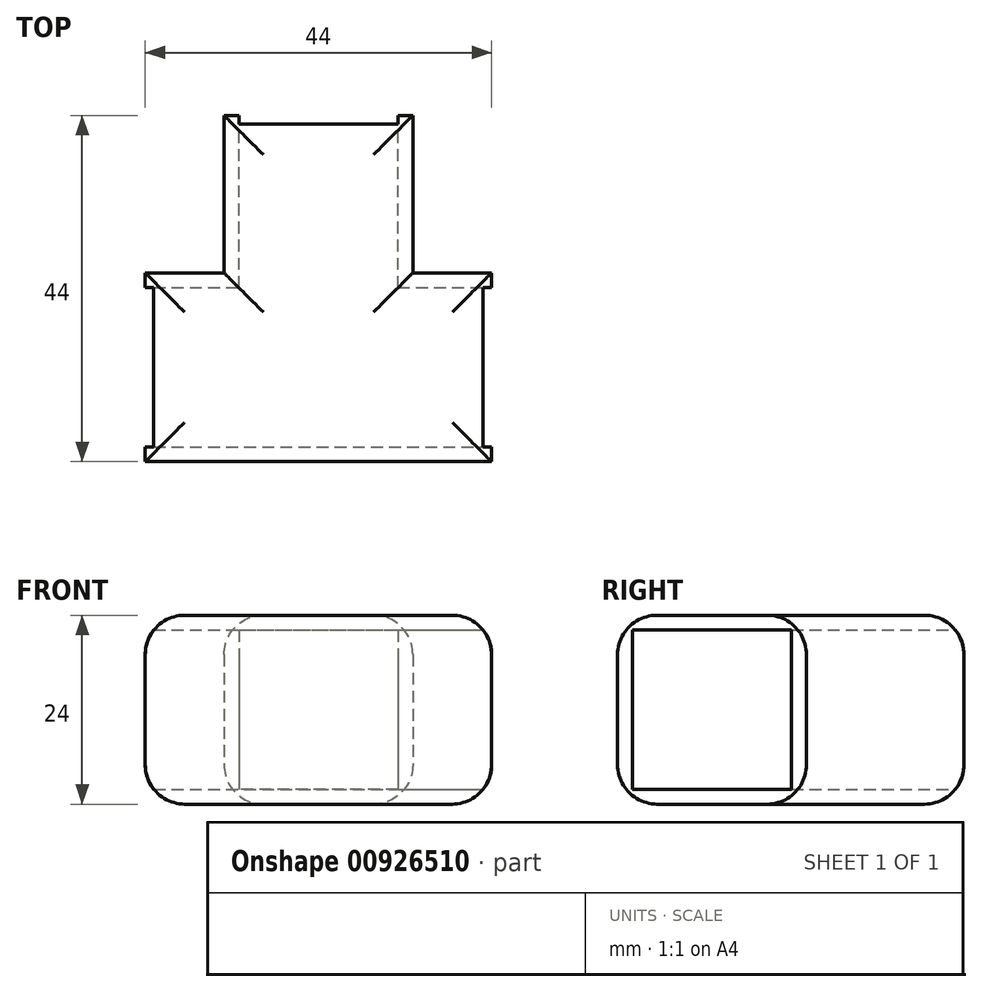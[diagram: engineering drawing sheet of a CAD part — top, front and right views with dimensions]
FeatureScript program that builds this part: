
annotation { "Feature Type Name" : "Feature", "Feature Type Description" : "" }
export const myFeature = defineFeature(function(context is Context, id is Id, definition is map)
    precondition{}
    {
        {
            var Q0;
            Q0=qCreatedBy(makeId("Top.planeOp"),FACE);
            var sketch = newSketch(context, id + "F0", { "sketchPlane" : qUnion([Q0])});
            skLineSegment(sketch, "E0.bottom", {"start": v(12.88, 0) * mm, "end": v(-11.12, 0) * mm});
            skLineSegment(sketch, "E0.top", {"start": v(12.88, 44) * mm, "end": v(-11.12, 44) * mm});
            skLineSegment(sketch, "E0.left", {"start": v(12.88, 0) * mm, "end": v(12.88, 44) * mm});
            skLineSegment(sketch, "E0.right", {"start": v(-11.12, 0) * mm, "end": v(-11.12, 44) * mm});
            skLineSegment(sketch, "E1.bottom", {"start": v(-21.12, 24) * mm, "end": v(22.88, 24) * mm});
            skLineSegment(sketch, "E1.top", {"start": v(-21.12, 0) * mm, "end": v(22.88, 0) * mm});
            skLineSegment(sketch, "E1.left", {"start": v(-21.12, 24) * mm, "end": v(-21.12, 0) * mm});
            skLineSegment(sketch, "E1.right", {"start": v(22.88, 24) * mm, "end": v(22.88, 0) * mm});
            skSolve(sketch);
        }
        {
            var Q0;
            {var subQ5=sQuery(id+"F0.wireOp",EDGE,"E1.left");Q0=makeQuery(id+"F0.imprint","IMPRINT",FACE,{"disambiguationData":[TD([[makeQuery(id+"F0.imprint","IMPRINT",EDGE,{"derivedFrom":subQ5}),1.0]])]});}
            var Q1;
            {var subQ0=sQuery(id+"F0.wireOp",EDGE,"E0.bottom");Q1=makeQuery(id+"F0.imprint","IMPRINT",FACE,{"disambiguationData":[TD([[makeQuery(id+"F0.imprint","IMPRINT",EDGE,{"derivedFrom":subQ0}),-1.0]])]});}
            var Q2;
            {var subQ5=sQuery(id+"F0.wireOp",EDGE,"E1.right");Q2=makeQuery(id+"F0.imprint","IMPRINT",FACE,{"disambiguationData":[TD([[makeQuery(id+"F0.imprint","IMPRINT",EDGE,{"derivedFrom":subQ5}),-1.0]])]});}
            var Q3;
            {var subQ0=sQuery(id+"F0.wireOp",EDGE,"E0.top");Q3=makeQuery(id+"F0.imprint","IMPRINT",FACE,{"disambiguationData":[TD([[makeQuery(id+"F0.imprint","IMPRINT",EDGE,{"derivedFrom":subQ0}),1.0]])]});}
            extrude(context, id + "F1", {"entities" : qUnion([Q0, Q1, Q2, Q3]), "depth" : 24 * mm, "offsetDistance" : 25 * mm});
        }
        {
            var Q0;
            Q0=makeQuery(id+"F1.opExtrude","SWEPT_FACE",FACE,{"disambiguationData":[OSD([sQuery(id+"F0.wireOp",EDGE,"E1.left")])]});
            var Q1;
            Q1=makeQuery(id+"F1.opExtrude","SWEPT_FACE",FACE,{"disambiguationData":[OSD([sQuery(id+"F0.wireOp",EDGE,"E1.right")])]});
            var Q2;
            Q2=makeQuery(id+"F1.opExtrude","SWEPT_FACE",FACE,{"disambiguationData":[OSD([sQuery(id+"F0.wireOp",EDGE,"E0.top")])]});
            shell(context, id + "F2", {"entities" : qUnion([Q0, Q1, Q2]), "thickness" : 1.9 * mm});
        }
        {
            var Q0;
            Q0=makeQuery(id+"F1.opExtrude","CAP_FACE",FACE,{"disambiguationData":[OSD([sQuery(id+"F0.wireOp",EDGE,"E0.bottom"),sQuery(id+"F0.wireOp",EDGE,"E0.top"),sQuery(id+"F0.wireOp",EDGE,"E0.left"),sQuery(id+"F0.wireOp",EDGE,"E0.right"),sQuery(id+"F0.wireOp",EDGE,"E1.bottom"),sQuery(id+"F0.wireOp",EDGE,"E1.top"),sQuery(id+"F0.wireOp",EDGE,"E1.left"),sQuery(id+"F0.wireOp",EDGE,"E1.right")])],"isStart":false});
            var Q1;
            Q1=makeQuery(id+"F1.opExtrude","CAP_FACE",FACE,{"disambiguationData":[OSD([sQuery(id+"F0.wireOp",EDGE,"E0.bottom"),sQuery(id+"F0.wireOp",EDGE,"E0.top"),sQuery(id+"F0.wireOp",EDGE,"E0.left"),sQuery(id+"F0.wireOp",EDGE,"E0.right"),sQuery(id+"F0.wireOp",EDGE,"E1.bottom"),sQuery(id+"F0.wireOp",EDGE,"E1.top"),sQuery(id+"F0.wireOp",EDGE,"E1.left"),sQuery(id+"F0.wireOp",EDGE,"E1.right")])],"isStart":true});
            fillet(context, id + "F3", {"entities" : qUnion([Q0, Q1]), "radius" : 5 * mm, "tangentPropagation" : true, "allowEdgeOverflow" : false});
        }
    });
